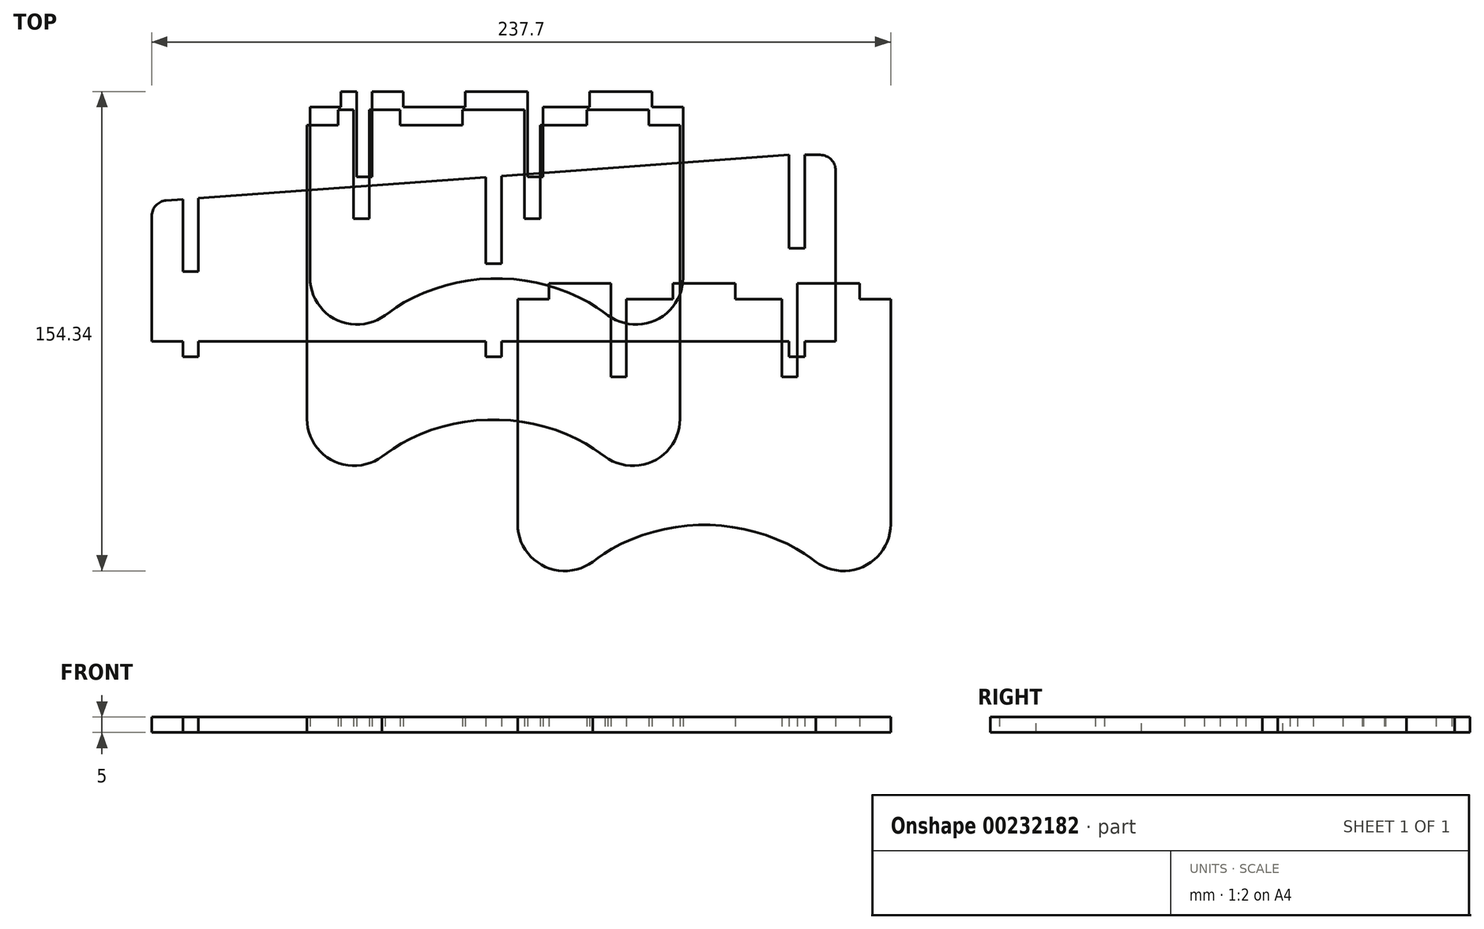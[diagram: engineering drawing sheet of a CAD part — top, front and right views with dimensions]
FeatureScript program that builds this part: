
annotation { "Feature Type Name" : "Feature", "Feature Type Description" : "" }
export const myFeature = defineFeature(function(context is Context, id is Id, definition is map)
    precondition{}
    {
        {
            assignVariable(context, id + "F0", {"name" : "plywoodThickness", "anyValue" : 5});
        }
        {
            var Q0;
            Q0=qCreatedBy(makeId("Top.planeOp"),FACE);
            var sketch = newSketch(context, id + "F1", { "sketchPlane" : qUnion([Q0])});
            skFitSpline(sketch, "E0.0", {"points": [v(35.77, -67.1) * mm, v(33.19, -65.23) * mm, v(27.73, -61.88) * mm, v(18.85, -58.2) * mm, v(9.5, -55.96) * mm, v(-0.08, -55.2) * mm, v(-9.66, -55.96) * mm, v(-19, -58.2) * mm, v(-27.89, -61.88) * mm, v(-33.35, -65.23) * mm, v(-35.93, -67.1) * mm]});
            skEllipticalArc(sketch, "E0.1", {});
            skLineSegment(sketch, "E0.2", {"start": v(-60.08, -55.01) * mm, "end": v(-60.08, 39.55) * mm});
            skLineSegment(sketch, "E0.3", {"start": v(-60.08, 39.55) * mm, "end": v(-50.08, 39.55) * mm});
            skLineSegment(sketch, "E0.4", {"start": v(59.92, -55.01) * mm, "end": v(59.92, 39.55) * mm});
            skEllipticalArc(sketch, "E0.5", {});
            skLineSegment(sketch, "E1", {"start": v(59.92, 39.55) * mm, "end": v(49.92, 39.55) * mm, "construction": true});
            skLineSegment(sketch, "E2", {"start": v(49.92, 39.55) * mm, "end": v(49.92, 44.55) * mm});
            skLineSegment(sketch, "E3", {"start": v(49.92, 44.55) * mm, "end": v(29.92, 44.55) * mm});
            skLineSegment(sketch, "E4", {"start": v(29.92, 44.55) * mm, "end": v(29.92, 39.55) * mm});
            skLineSegment(sketch, "E5", {"start": v(29.92, 39.55) * mm, "end": v(14.92, 39.55) * mm});
            skLineSegment(sketch, "E6", {"start": v(9.92, 39.55) * mm, "end": v(9.92, 44.55) * mm});
            skLineSegment(sketch, "E7", {"start": v(9.92, 44.55) * mm, "end": v(-10.08, 44.55) * mm});
            skLineSegment(sketch, "E8", {"start": v(-10.08, 44.55) * mm, "end": v(-10.08, 39.55) * mm});
            skLineSegment(sketch, "E9", {"start": v(-30.08, 39.55) * mm, "end": v(-30.08, 44.55) * mm});
            skLineSegment(sketch, "E10.trimOffspring", {"start": v(49.92, 39.55) * mm, "end": v(59.92, 39.55) * mm});
            skLineSegment(sketch, "E11.trimOffspring", {"start": v(14.92, 39.55) * mm, "end": v(29.92, 39.55) * mm});
            skLineSegment(sketch, "E12", {"start": v(-50.08, 39.55) * mm, "end": v(-50.08, 44.55) * mm});
            skLineSegment(sketch, "E13", {"start": v(-50.08, 44.55) * mm, "end": v(-45.08, 44.55) * mm});
            skLineSegment(sketch, "E14", {"start": v(-30.08, 39.55) * mm, "end": v(-10.08, 39.55) * mm});
            skLineSegment(sketch, "E15", {"start": v(-60.08, 39.55) * mm, "end": v(-45.08, 39.55) * mm, "construction": true});
            skLineSegment(sketch, "E16", {"start": v(-45.08, 39.55) * mm, "end": v(-45.08, 44.55) * mm});
            skLineSegment(sketch, "E17", {"start": v(-40.08, 44.55) * mm, "end": v(-40.08, 9.55) * mm});
            skLineSegment(sketch, "E18", {"start": v(-40.08, 9.55) * mm, "end": v(-45.08, 9.55) * mm});
            skLineSegment(sketch, "E19", {"start": v(-45.08, 9.55) * mm, "end": v(-45.08, 39.55) * mm});
            skLineSegment(sketch, "E20.trimOffspring", {"start": v(-40.08, 44.55) * mm, "end": v(-30.08, 44.55) * mm});
            skLineSegment(sketch, "E21", {"start": v(-40.08, 9.55) * mm, "end": v(9.92, 9.55) * mm, "construction": true});
            skLineSegment(sketch, "E22", {"start": v(9.92, 39.55) * mm, "end": v(9.92, 9.55) * mm});
            skLineSegment(sketch, "E23", {"start": v(9.92, 9.55) * mm, "end": v(14.92, 9.55) * mm});
            skLineSegment(sketch, "E24", {"start": v(14.92, 9.55) * mm, "end": v(14.92, 39.55) * mm});
            const initialGuessF1  = {"E0.1": [-0.04491212090071209, -0.05501442365348339, -1, 0, 0.015167811312117512, 0.015, 0, 2.204346671821993], "E0.5": [0.044752256475053015, -0.055014423653483434, -1, 0, 0.015167811312117512, 0.015, 0.9372459817677954, 3.141592653589793]};
            skSetInitialGuess(sketch, initialGuessF1);
            skSolve(sketch);
        }
        {
            var Q0;
            Q0=qCreatedBy(makeId("Top.planeOp"),FACE);
            var sketch = newSketch(context, id + "F2", { "sketchPlane" : qUnion([Q0])});
            skFitSpline(sketch, "E25.0", {"points": [v(103.55, -100.99) * mm, v(100.97, -99.1) * mm, v(95.5, -95.76) * mm, v(86.63, -92.08) * mm, v(77.28, -89.84) * mm, v(67.7, -89.09) * mm, v(58.12, -89.84) * mm, v(48.77, -92.08) * mm, v(39.9, -95.76) * mm, v(34.43, -99.1) * mm, v(31.85, -100.99) * mm]});
            skEllipticalArc(sketch, "E25.1", {});
            skLineSegment(sketch, "E25.2", {"start": v(7.7, -88.9) * mm, "end": v(7.7, -16.4) * mm});
            skLineSegment(sketch, "E25.3", {"start": v(7.7, -16.4) * mm, "end": v(17.7, -16.4) * mm});
            skLineSegment(sketch, "E25.4", {"start": v(127.7, -88.9) * mm, "end": v(127.7, -16.4) * mm});
            skEllipticalArc(sketch, "E25.5", {});
            skLineSegment(sketch, "E26", {"start": v(127.7, -16.4) * mm, "end": v(117.7, -16.4) * mm, "construction": true});
            skLineSegment(sketch, "E27", {"start": v(117.7, -16.4) * mm, "end": v(117.7, -11.4) * mm});
            skLineSegment(sketch, "E28", {"start": v(117.7, -11.4) * mm, "end": v(97.7, -11.4) * mm});
            skLineSegment(sketch, "E29", {"start": v(92.7, -16.4) * mm, "end": v(77.7, -16.4) * mm});
            skLineSegment(sketch, "E30", {"start": v(77.7, -16.4) * mm, "end": v(77.7, -11.4) * mm});
            skLineSegment(sketch, "E31", {"start": v(57.7, -11.4) * mm, "end": v(57.7, -16.4) * mm});
            skLineSegment(sketch, "E32.trimOffspring", {"start": v(117.7, -16.4) * mm, "end": v(127.7, -16.4) * mm});
            skLineSegment(sketch, "E33.trimOffspring", {"start": v(77.7, -16.4) * mm, "end": v(92.7, -16.4) * mm});
            skLineSegment(sketch, "E34", {"start": v(17.7, -16.4) * mm, "end": v(17.7, -11.4) * mm});
            skLineSegment(sketch, "E35", {"start": v(57.7, -16.4) * mm, "end": v(57.7, -11.4) * mm});
            skLineSegment(sketch, "E36", {"start": v(17.7, -11.4) * mm, "end": v(37.7, -11.4) * mm});
            skLineSegment(sketch, "E37", {"start": v(42.7, -16.4) * mm, "end": v(57.7, -16.4) * mm});
            skLineSegment(sketch, "E38", {"start": v(57.7, -11.4) * mm, "end": v(77.7, -11.4) * mm});
            skLineSegment(sketch, "E39", {"start": v(42.7, -16.4) * mm, "end": v(42.7, -41.4) * mm});
            skLineSegment(sketch, "E40", {"start": v(42.7, -41.4) * mm, "end": v(37.7, -41.4) * mm});
            skLineSegment(sketch, "E41", {"start": v(37.7, -41.4) * mm, "end": v(37.7, -11.4) * mm});
            skLineSegment(sketch, "E42", {"start": v(92.7, -16.4) * mm, "end": v(92.7, -41.4) * mm});
            skLineSegment(sketch, "E43", {"start": v(92.7, -41.4) * mm, "end": v(97.7, -41.4) * mm});
            skLineSegment(sketch, "E44", {"start": v(97.7, -41.4) * mm, "end": v(97.7, -11.4) * mm});
            const initialGuessF2  = {"E25.1": [0.022866553700465433, -0.08889646411413127, -1, 0, 0.015167811312117512, 0.015, 0, 2.204346671821993], "E25.5": [0.11253093107623048, -0.08889646411413131, -1, 0, 0.015167811312117512, 0.015, 0.9372459817677956, 3.141592653589793]};
            skSetInitialGuess(sketch, initialGuessF2);
            skSolve(sketch);
        }
        {
            var Q0;
            Q0=qCreatedBy(makeId("Top.planeOp"),FACE);
            var sketch = newSketch(context, id + "F3", { "sketchPlane" : qUnion([Q0])});
            skLineSegment(sketch, "E45.bottom", {"start": v(110, -30) * mm, "end": v(100, -30) * mm});
            skLineSegment(sketch, "E45.top", {"start": v(105, 30) * mm, "end": v(100, 30) * mm});
            skLineSegment(sketch, "E45.left", {"start": v(110, -30) * mm, "end": v(110, 25) * mm});
            skLineSegment(sketch, "E45.right", {"start": v(-110, -30) * mm, "end": v(-110, 10.35) * mm});
            skPoint(sketch, "E45.middle", {"position": v(0, 0) * mm});
            skLineSegment(sketch, "E46", {"start": v(0, 0) * mm, "end": v(-2.5, 0) * mm, "construction": true});
            skLineSegment(sketch, "E47", {"start": v(-100, 15.73) * mm, "end": v(-100, -7.5) * mm});
            skLineSegment(sketch, "E48", {"start": v(-100, -7.5) * mm, "end": v(-95, -7.5) * mm});
            skLineSegment(sketch, "E49", {"start": v(-95, -7.5) * mm, "end": v(-95, 16.1) * mm});
            skLineSegment(sketch, "E50", {"start": v(-2.5, 22.87) * mm, "end": v(-2.5, -5) * mm});
            skLineSegment(sketch, "E51", {"start": v(-2.5, -5) * mm, "end": v(2.5, -5) * mm});
            skLineSegment(sketch, "E52", {"start": v(2.5, -5) * mm, "end": v(2.5, 23.23) * mm});
            skLineSegment(sketch, "E53", {"start": v(110, 30) * mm, "end": v(100, 30) * mm, "construction": true});
            skLineSegment(sketch, "E54", {"start": v(100, 30) * mm, "end": v(100, 0) * mm});
            skLineSegment(sketch, "E55", {"start": v(100, 0) * mm, "end": v(95, 0) * mm});
            skLineSegment(sketch, "E56", {"start": v(95, 0) * mm, "end": v(95, 30) * mm});
            skLineSegment(sketch, "E57", {"start": v(100, -30) * mm, "end": v(100, -35) * mm});
            skLineSegment(sketch, "E58", {"start": v(100, -35) * mm, "end": v(95, -35) * mm});
            skLineSegment(sketch, "E59", {"start": v(95, -35) * mm, "end": v(95, -30) * mm});
            skLineSegment(sketch, "E60", {"start": v(2.5, -30) * mm, "end": v(2.5, -35) * mm});
            skLineSegment(sketch, "E61", {"start": v(2.5, -35) * mm, "end": v(-2.5, -35) * mm});
            skLineSegment(sketch, "E62", {"start": v(-2.5, -35) * mm, "end": v(-2.5, -30) * mm});
            skLineSegment(sketch, "E63", {"start": v(-100, -30) * mm, "end": v(-100, -35) * mm});
            skLineSegment(sketch, "E64", {"start": v(-100, -35) * mm, "end": v(-95, -35) * mm});
            skLineSegment(sketch, "E65", {"start": v(-95, -35) * mm, "end": v(-95, -30) * mm});
            skLineSegment(sketch, "E66.trimOffspring", {"start": v(95, -30) * mm, "end": v(2.5, -30) * mm});
            skLineSegment(sketch, "E67.trimOffspring", {"start": v(-2.5, -30) * mm, "end": v(-95, -30) * mm});
            skLineSegment(sketch, "E68.trimOffspring", {"start": v(-100, -30) * mm, "end": v(-110, -30) * mm});
            skPoint(sketch, "E69.visualSharp", {"position": v(110, 30) * mm});
            skArc(sketch, "E69.filletArc", {"start": v(110, 25) * mm, "mid": v(108.54, 28.54) * mm, "end": v(105, 30) * mm});
            skLineSegment(sketch, "E70", {"start": v(-110, -30) * mm, "end": v(-110, 15) * mm, "construction": true});
            skLineSegment(sketch, "E71", {"start": v(-105.36, 15.34) * mm, "end": v(-100, 15.73) * mm});
            skLineSegment(sketch, "E72.trimOffspring", {"start": v(-95, 16.1) * mm, "end": v(-2.5, 22.87) * mm});
            skLineSegment(sketch, "E73.trimOffspring", {"start": v(2.5, 23.23) * mm, "end": v(95, 30) * mm});
            skPoint(sketch, "E74.visualSharp", {"position": v(-110, 15) * mm});
            skArc(sketch, "E74.filletArc", {"start": v(-105.36, 15.34) * mm, "mid": v(-108.66, 13.76) * mm, "end": v(-110, 10.35) * mm});
            skSolve(sketch);
        }
        {
            var Q0;
            Q0=qCreatedBy(makeId("Top.planeOp"),FACE);
            var sketch = newSketch(context, id + "F4", { "sketchPlane" : qUnion([Q0])});
            skFitSpline(sketch, "E75.0", {"points": [v(36.74, -21.65) * mm, v(34.15, -19.77) * mm, v(28.7, -16.42) * mm, v(19.81, -12.75) * mm, v(10.47, -10.5) * mm, v(0.88, -9.75) * mm, v(-8.7, -10.5) * mm, v(-18.04, -12.75) * mm, v(-26.92, -16.42) * mm, v(-32.38, -19.77) * mm, v(-34.97, -21.65) * mm]});
            skEllipticalArc(sketch, "E75.1", {});
            skLineSegment(sketch, "E75.2", {"start": v(-59.12, -9.56) * mm, "end": v(-59.12, 45.44) * mm});
            skLineSegment(sketch, "E75.3", {"start": v(-59.12, 45.44) * mm, "end": v(-49.12, 45.44) * mm});
            skLineSegment(sketch, "E75.4", {"start": v(60.88, -9.56) * mm, "end": v(60.88, 45.44) * mm});
            skEllipticalArc(sketch, "E75.5", {});
            skLineSegment(sketch, "E76", {"start": v(60.88, 45.44) * mm, "end": v(50.88, 45.44) * mm, "construction": true});
            skLineSegment(sketch, "E77", {"start": v(50.88, 45.44) * mm, "end": v(50.88, 50.44) * mm});
            skLineSegment(sketch, "E78", {"start": v(50.88, 50.44) * mm, "end": v(30.88, 50.44) * mm});
            skLineSegment(sketch, "E79", {"start": v(30.88, 50.44) * mm, "end": v(30.88, 45.44) * mm});
            skLineSegment(sketch, "E80", {"start": v(30.88, 45.44) * mm, "end": v(15.88, 45.44) * mm});
            skLineSegment(sketch, "E81", {"start": v(10.88, 45.44) * mm, "end": v(10.88, 50.44) * mm});
            skLineSegment(sketch, "E82", {"start": v(10.88, 50.44) * mm, "end": v(-9.12, 50.44) * mm});
            skLineSegment(sketch, "E83", {"start": v(-9.12, 50.44) * mm, "end": v(-9.12, 45.44) * mm});
            skLineSegment(sketch, "E84", {"start": v(-29.12, 45.44) * mm, "end": v(-29.12, 50.44) * mm});
            skLineSegment(sketch, "E85.trimOffspring", {"start": v(50.88, 45.44) * mm, "end": v(60.88, 45.44) * mm});
            skLineSegment(sketch, "E86.trimOffspring", {"start": v(15.88, 45.44) * mm, "end": v(30.88, 45.44) * mm});
            skLineSegment(sketch, "E87", {"start": v(-49.12, 45.44) * mm, "end": v(-49.12, 50.44) * mm});
            skLineSegment(sketch, "E88", {"start": v(-49.12, 50.44) * mm, "end": v(-44.12, 50.44) * mm});
            skLineSegment(sketch, "E89", {"start": v(-29.12, 45.44) * mm, "end": v(-9.12, 45.44) * mm});
            skLineSegment(sketch, "E90", {"start": v(-59.12, 45.44) * mm, "end": v(-44.12, 45.44) * mm, "construction": true});
            skLineSegment(sketch, "E91", {"start": v(-44.12, 45.44) * mm, "end": v(-44.12, 50.44) * mm});
            skLineSegment(sketch, "E92", {"start": v(-39.12, 50.44) * mm, "end": v(-39.12, 22.94) * mm});
            skLineSegment(sketch, "E93", {"start": v(-39.12, 22.94) * mm, "end": v(-44.12, 22.94) * mm});
            skLineSegment(sketch, "E94", {"start": v(-44.12, 22.94) * mm, "end": v(-44.12, 45.44) * mm});
            skLineSegment(sketch, "E95.trimOffspring", {"start": v(-39.12, 50.44) * mm, "end": v(-29.12, 50.44) * mm});
            skLineSegment(sketch, "E96", {"start": v(-39.12, 22.94) * mm, "end": v(10.88, 22.94) * mm, "construction": true});
            skLineSegment(sketch, "E97", {"start": v(10.88, 45.44) * mm, "end": v(10.88, 22.94) * mm});
            skLineSegment(sketch, "E98", {"start": v(10.88, 22.94) * mm, "end": v(15.88, 22.94) * mm});
            skLineSegment(sketch, "E99", {"start": v(15.88, 22.94) * mm, "end": v(15.88, 45.44) * mm});
            const initialGuessF4  = {"E75.1": [-0.043947227189132465, -0.009560512197658352, -1, 0, 0.015167811312117512, 0.015, 0, 2.2043466718219933], "E75.5": [0.04571715018663264, -0.009560512197658393, -1, 0, 0.015167811312117512, 0.015, 0.9372459817677955, 3.141592653589793]};
            skSetInitialGuess(sketch, initialGuessF4);
            skSolve(sketch);
        }
        {
            var Q0;
            Q0 = qSketchRegion(id + "F1", true);
            extrude(context, id + "F5", {"entities" : qUnion([Q0]), "depth" : (getVariable(context, 'plywoodThickness')) * mm});
        }
        {
            var Q0;
            Q0 = qSketchRegion(id + "F2", true);
            extrude(context, id + "F6", {"entities" : qUnion([Q0]), "depth" : (getVariable(context, 'plywoodThickness')) * mm});
        }
        {
            var Q0;
            Q0 = qSketchRegion(id + "F4", true);
            extrude(context, id + "F7", {"entities" : qUnion([Q0]), "depth" : (getVariable(context, 'plywoodThickness')) * mm});
        }
        {
            var Q0;
            Q0 = qSketchRegion(id + "F3", true);
            extrude(context, id + "F8", {"entities" : qUnion([Q0]), "depth" : (getVariable(context, 'plywoodThickness')) * mm});
        }
    });
